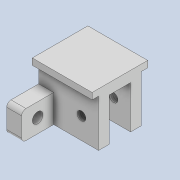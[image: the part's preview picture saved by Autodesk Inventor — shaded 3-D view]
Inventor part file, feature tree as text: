
AUTODESK INVENTOR PART (.ipt)
format: ipt  version: 2020 (Build 240168000, 168)  size: 189,952 bytes
history: native  units: mm
features: extrude x4, sketch x4, hole x1, fillet x1
ambient origin geometry x8: Origin, YZ Plane, XZ Plane, XY Plane, X Axis, Y Axis, Z Axis, Center Point
bodies: Solid1 (feature_tree)
feature tree (10):
  extrude  "Extrusion4"  Depth=25.0mm
  sketch  "Sketch15"  dims[d28=28.0mm d29=0.0mm d30=3.0mm]
  extrude  "Extrusion8"  Depth=3.0mm
  hole  "Hole6"  [1 undecoded]
  extrude  "Extrusion9"  TaperAngle=0.0deg  [1 undecoded]
  fillet  "Fillet1"  Radius=10.0mm
  extrude  "Extrusion10"  Depth=21.0mm
  sketch  "Sketch14"  dims[d26=20.0mm d27=25.0mm]
  sketch  "Sketch16"  dims[d31=3.0mm d32=3.0mm]
  sketch  "Sketch17"  dims[d33=3.0mm d72=0.0mm d73=10.0mm d74=21.0mm d75=20.0mm d76=0.0mm d78=8.0mm d79=4.134mm d80=10.0mm d81=4.0mm d82=2.0mm d83=90.0deg d84=8.0mm d85=20.594885mm d86=15.0mm d88=15.0mm d89=13.0mm d90=5.0mm d91=7.5mm d92=7.5mm d93=7.0mm d94=0.0mm d96=2.0mm d98=10.0mm d99=9.0mm d100=2.0mm d101=0.0mm]
note: 2 required parameter values undecoded (feature->parameter linkage not recoverable at this tier; creation-order binding heuristic only, values carry confidence <= 0.55)
